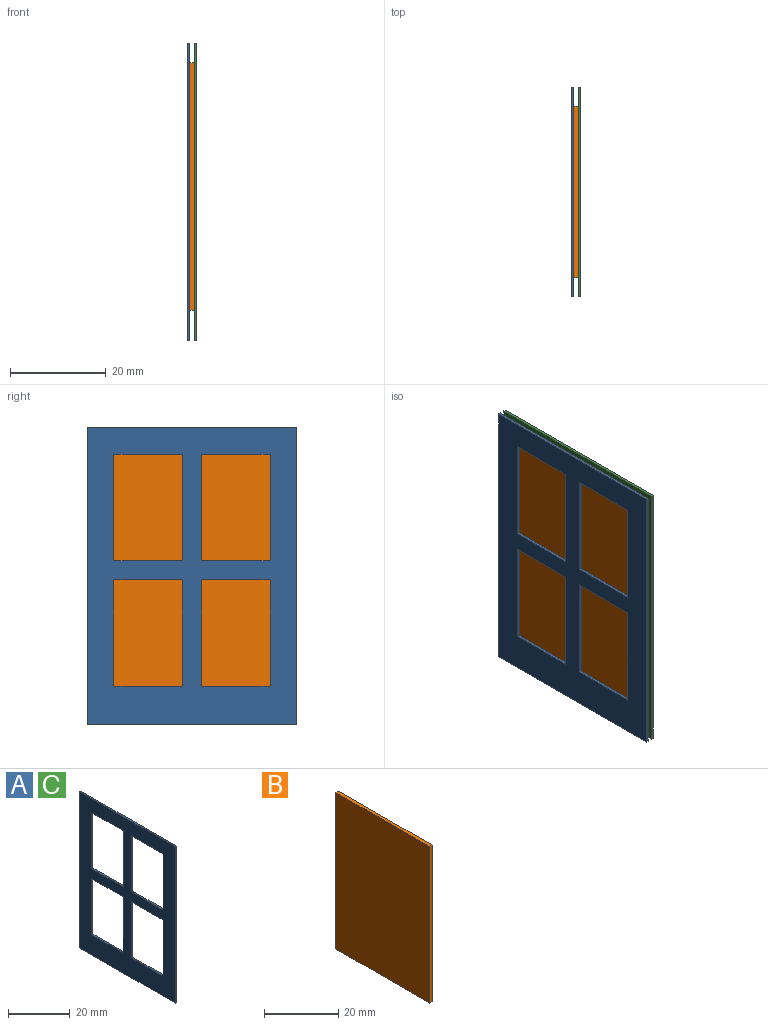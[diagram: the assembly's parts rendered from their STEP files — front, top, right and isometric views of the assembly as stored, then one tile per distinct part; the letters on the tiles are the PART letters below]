
ASSEMBLY  parts=3 mates=2
PART A: 22 faces, bbox 0.5x43.7x61.9 mm
  f0: plane 43.66x0.51mm, normal (0,0,1), area 22.2mm2, adj f1,f19,f20,f21
  f1: plane 61.91x0.51mm, normal (0,-1,0), area 31.5mm2, adj f0,f2,f20,f21
  f2: plane 43.66x0.51mm, normal (0,0,-1), area 22.2mm2, adj f1,f19,f20,f21
  f3: plane 22.23x0.51mm, normal (0,1,0), area 11.3mm2, adj f4,f15,f20,f21
  f4: plane 14.29x0.51mm, normal (0,0,-1), area 7.3mm2, adj f3,f5,f20,f21
  f5: plane 22.23x0.51mm, normal (0,-1,0), area 11.3mm2, adj f4,f15,f20,f21
  f6: plane 22.23x0.51mm, normal (0,1,0), area 11.3mm2, adj f7,f16,f20,f21
  f7: plane 14.29x0.51mm, normal (0,0,-1), area 7.3mm2, adj f6,f8,f20,f21
  f8: plane 22.23x0.51mm, normal (0,-1,0), area 11.3mm2, adj f7,f16,f20,f21
  f9: plane 22.23x0.51mm, normal (0,1,0), area 11.3mm2, adj f10,f17,f20,f21
  f10: plane 14.29x0.51mm, normal (0,0,-1), area 7.3mm2, adj f9,f11,f20,f21
  f11: plane 22.23x0.51mm, normal (0,-1,0), area 11.3mm2, adj f10,f17,f20,f21
  f12: plane 22.23x0.51mm, normal (0,1,0), area 11.3mm2, adj f13,f18,f20,f21
  f13: plane 14.29x0.51mm, normal (0,0,-1), area 7.3mm2, adj f12,f14,f20,f21
  f14: plane 22.23x0.51mm, normal (0,-1,0), area 11.3mm2, adj f13,f18,f20,f21
  f15: plane 14.29x0.51mm, normal (0,0,1), area 7.3mm2, adj f3,f5,f20,f21
  f16: plane 14.29x0.51mm, normal (0,0,1), area 7.3mm2, adj f6,f8,f20,f21
  f17: plane 14.29x0.51mm, normal (0,0,1), area 7.3mm2, adj f9,f11,f20,f21
  f18: plane 14.29x0.51mm, normal (0,0,1), area 7.3mm2, adj f12,f14,f20,f21
  f19: plane 61.91x0.51mm, normal (0,1,0), area 31.5mm2, adj f0,f2,f20,f21
  f20: plane 61.91x43.66mm, normal (1,0,0), area 1432.7mm2, adj f0,f1,f2,f3,f4,f5,f6,f7
  f21: plane 61.91x43.66mm, normal (-1,0,0), area 1432.7mm2, adj f0,f1,f2,f3,f4,f5,f6,f7
PART B: 6 faces, bbox 1x35.7x51.6 mm
  f0: plane 35.72x1.02mm, normal (0,0,1), area 36.3mm2, adj f1,f3,f4,f5
  f1: plane 51.59x1.02mm, normal (0,1,0), area 52.4mm2, adj f0,f2,f4,f5
  f2: plane 35.72x1.02mm, normal (0,0,-1), area 36.3mm2, adj f1,f3,f4,f5
  f3: plane 51.59x1.02mm, normal (0,-1,0), area 52.4mm2, adj f0,f2,f4,f5
  f4: plane 51.59x35.72mm, normal (-1,0,0), area 1842.9mm2, adj f0,f1,f2,f3
  f5: plane 51.59x35.72mm, normal (1,0,0), area 1842.9mm2, adj f0,f1,f2,f3
PART C: same geometry as A
PLACE A t=(-14.53,-10.11,0.93)mm
PLACE B t=(-13,-10.11,0.93)mm
PLACE C t=(-13,-10.11,0.93)mm
MATE fastened B.f5 <-> C.f21  axis (1,0,0) through (-13,11.72,58.87)mm
MATE fastened B.f4 <-> A.f20  axis (-1,0,0) through (-14.02,11.72,58.87)mm
